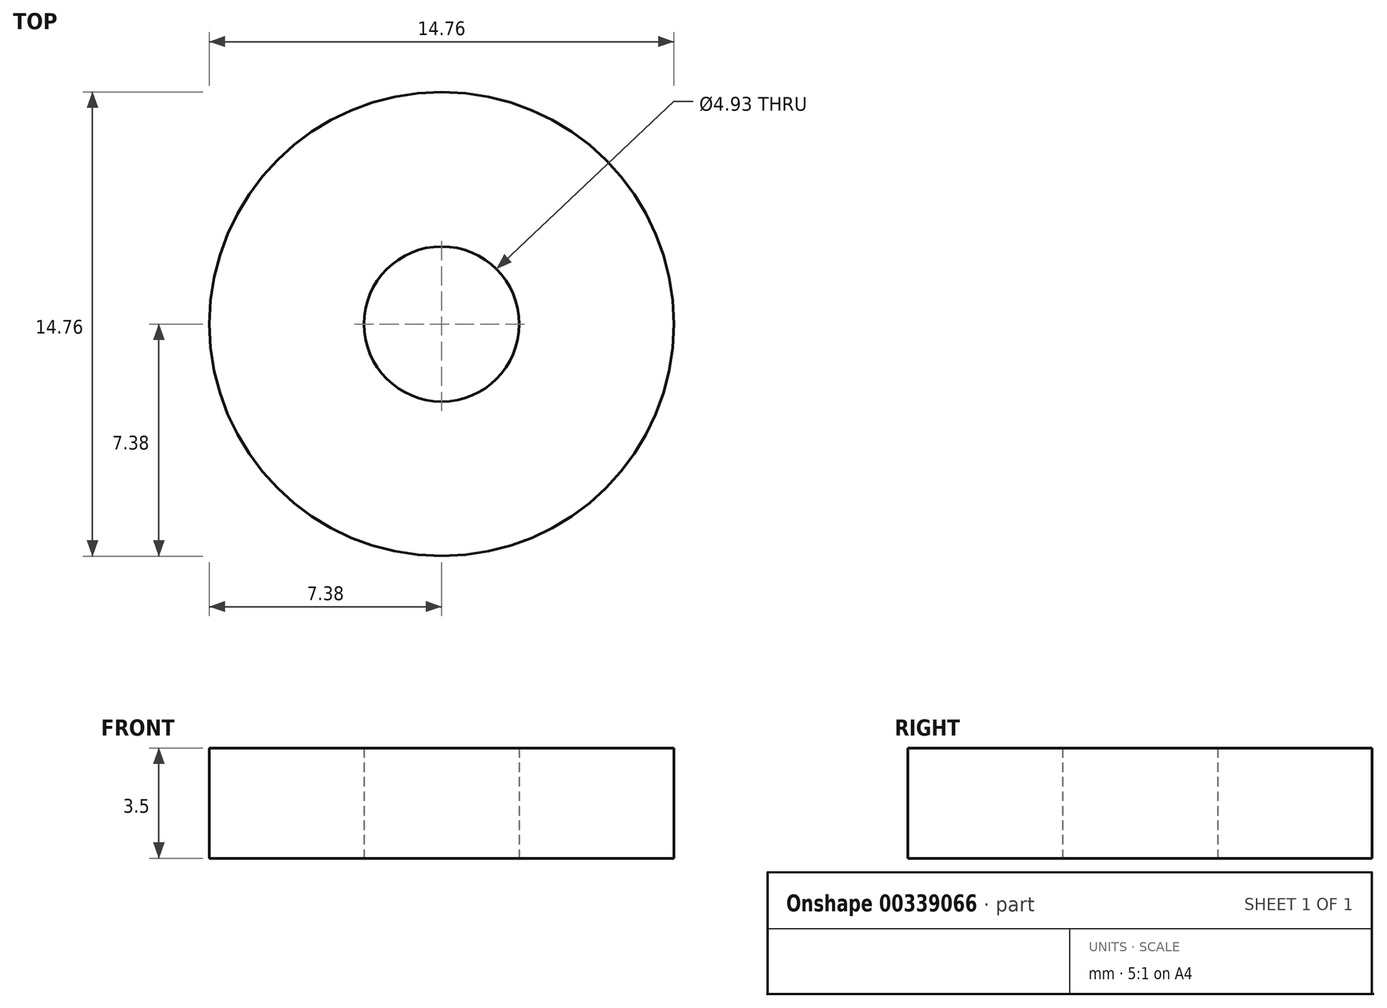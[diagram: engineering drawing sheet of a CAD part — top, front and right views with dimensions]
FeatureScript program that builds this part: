
annotation { "Feature Type Name" : "Feature", "Feature Type Description" : "" }
export const myFeature = defineFeature(function(context is Context, id is Id, definition is map)
    precondition{}
    {
        {
            var Q0;
            Q0=qCreatedBy(makeId("Top.planeOp"),FACE);
            var sketch = newSketch(context, id + "F0", { "sketchPlane" : qUnion([Q0])});
            skCircle(sketch, "E0", {"center": v(0, 0) * mm, "radius": 7.38 * mm});
            skCircle(sketch, "E1", {"center": v(0, 0) * mm, "radius": 2.46 * mm});
            skSolve(sketch);
        }
        {
            var Q0;
            Q0=makeQuery(id+"F0.imprint","IMPRINT",FACE,{"disambiguationData":[TD([[makeQuery(id+"F0.imprint","IMPRINT",EDGE,{"derivedFrom":sQuery(id+"F0.wireOp",EDGE,"E0")}),1.0]])]});
            extrude(context, id + "F1", {"entities" : qUnion([Q0]), "depth" : 3.5 * mm, "offsetDistance" : 25 * mm});
        }
    });
